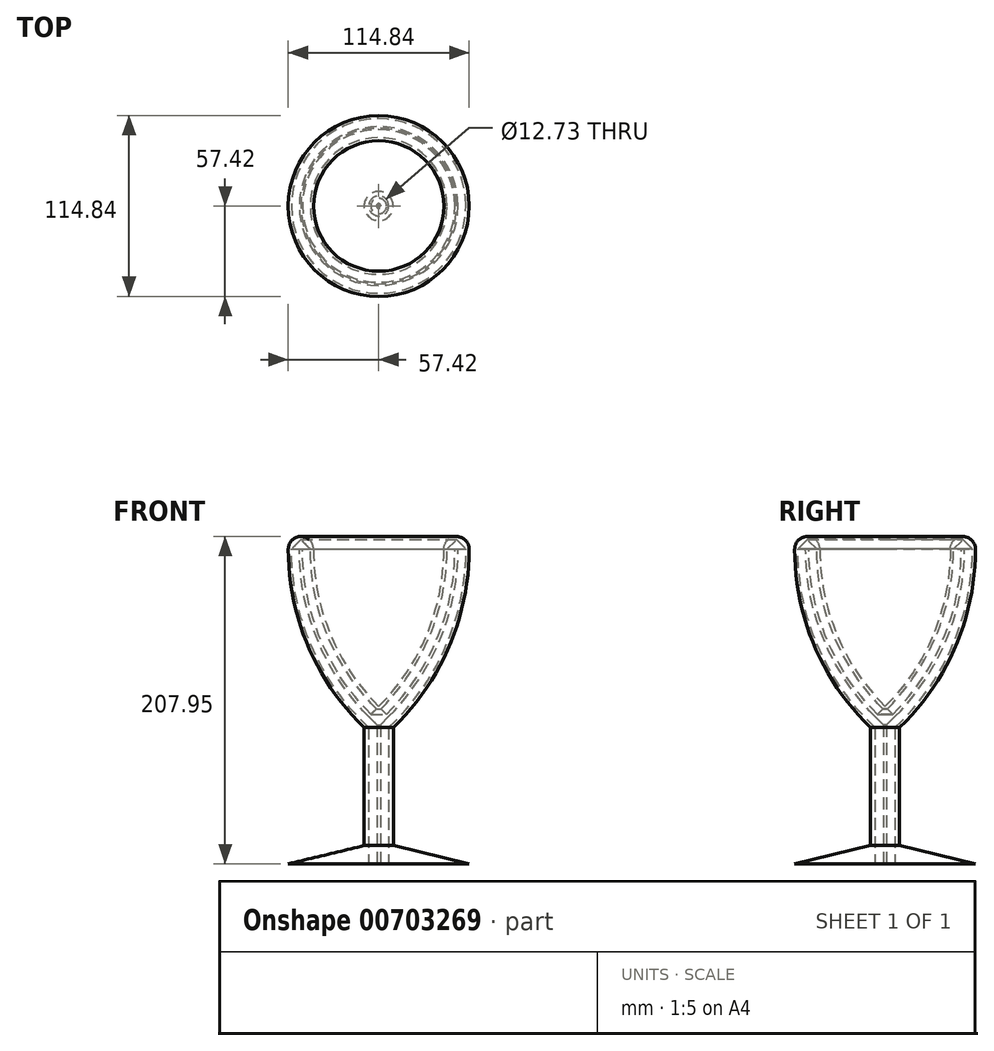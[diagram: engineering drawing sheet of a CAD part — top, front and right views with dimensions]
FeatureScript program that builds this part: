
annotation { "Feature Type Name" : "Feature", "Feature Type Description" : "" }
export const myFeature = defineFeature(function(context is Context, id is Id, definition is map)
    precondition{}
    {
        {
            var Q0;
            Q0=qCreatedBy(makeId("Front.planeOp"),FACE);
            var sketch = newSketch(context, id + "F0", { "sketchPlane" : qUnion([Q0])});
            skArc(sketch, "E0", {"start": v(-41.42, 100) * mm, "mid": v(-30.66, 45.88) * mm, "end": v(0, 0) * mm});
            skLineSegment(sketch, "E1", {"start": v(0, 0) * mm, "end": v(6.82, -6.82) * mm, "construction": true});
            skArc(sketch, "E2", {"start": v(0, 0) * mm, "mid": v(30.66, 45.88) * mm, "end": v(41.42, 100) * mm});
            skLineSegment(sketch, "E3", {"start": v(-100, 100) * mm, "end": v(0, 100) * mm, "construction": true});
            skLineSegment(sketch, "E4", {"start": v(0, 100) * mm, "end": v(100, 100) * mm, "construction": true});
            skArc(sketch, "E5.0", {"start": v(-43.42, 100) * mm, "mid": v(-32.5, 45.12) * mm, "end": v(-1.41, -1.41) * mm});
            skArc(sketch, "E6.0", {"start": v(1.41, -1.41) * mm, "mid": v(32.5, 45.12) * mm, "end": v(43.42, 100) * mm});
            skLineSegment(sketch, "E7", {"start": v(0, 0) * mm, "end": v(-1.41, -1.41) * mm, "construction": true});
            skLineSegment(sketch, "E8", {"start": v(0, 0) * mm, "end": v(1.41, -1.41) * mm, "construction": true});
            skLineSegment(sketch, "E9", {"start": v(-1.41, -1.41) * mm, "end": v(0, -1.41) * mm, "construction": true});
            skLineSegment(sketch, "E10", {"start": v(0, -1.41) * mm, "end": v(1.41, -1.41) * mm, "construction": true});
            skArc(sketch, "E11.0", {"start": v(-48.42, 100) * mm, "mid": v(-37.12, 43.2) * mm, "end": v(-4.95, -4.95) * mm});
            skArc(sketch, "E12.0", {"start": v(4.95, -4.95) * mm, "mid": v(37.12, 43.2) * mm, "end": v(48.42, 100) * mm});
            skArc(sketch, "E13.0", {"start": v(-50.42, 100) * mm, "mid": v(-38.97, 42.44) * mm, "end": v(-6.36, -6.36) * mm});
            skArc(sketch, "E14.0", {"start": v(6.36, -6.36) * mm, "mid": v(38.97, 42.44) * mm, "end": v(50.42, 100) * mm});
            skLineSegment(sketch, "E15", {"start": v(-1.41, -1.41) * mm, "end": v(-4.95, -4.95) * mm});
            skLineSegment(sketch, "E16", {"start": v(1.41, -1.41) * mm, "end": v(4.95, -4.95) * mm});
            skLineSegment(sketch, "E17", {"start": v(-4.95, -4.95) * mm, "end": v(-6.36, -6.36) * mm, "construction": true});
            skLineSegment(sketch, "E18", {"start": v(4.95, -4.95) * mm, "end": v(6.36, -6.36) * mm, "construction": true});
            skArc(sketch, "E19.0", {"start": v(-55.42, 100) * mm, "mid": v(-42.63, 38.26) * mm, "end": v(-6.36, -13.32) * mm});
            skArc(sketch, "E20.0", {"start": v(6.36, -13.32) * mm, "mid": v(42.63, 38.26) * mm, "end": v(55.42, 100) * mm});
            skArc(sketch, "E21.0", {"start": v(-57.42, 100) * mm, "mid": v(-44.88, 38.43) * mm, "end": v(-9.27, -13.32) * mm});
            skArc(sketch, "E22.0", {"start": v(9.27, -13.32) * mm, "mid": v(44.88, 38.43) * mm, "end": v(57.42, 100) * mm});
            skLineSegment(sketch, "E23", {"start": v(6.36, -6.36) * mm, "end": v(6.36, -13.32) * mm});
            skLineSegment(sketch, "E24", {"start": v(9.27, -13.32) * mm, "end": v(6.36, -13.32) * mm, "construction": true});
            skLineSegment(sketch, "E25", {"start": v(-6.36, -6.36) * mm, "end": v(-6.36, -13.32) * mm});
            skLineSegment(sketch, "E26", {"start": v(-9.27, -13.32) * mm, "end": v(-6.36, -13.32) * mm, "construction": true});
            skLineSegment(sketch, "E27", {"start": v(-55.42, 100) * mm, "end": v(-49.42, 106) * mm});
            skLineSegment(sketch, "E28", {"start": v(-49.42, 106) * mm, "end": v(-43.42, 100) * mm});
            skLineSegment(sketch, "E29", {"start": v(43.42, 100) * mm, "end": v(49.42, 106) * mm});
            skLineSegment(sketch, "E30", {"start": v(49.42, 106) * mm, "end": v(55.42, 100) * mm});
            skArc(sketch, "E31", {"start": v(-41.42, 100) * mm, "mid": v(-49.42, 108) * mm, "end": v(-57.42, 100) * mm});
            skLineSegment(sketch, "E32", {"start": v(-50.42, 100) * mm, "end": v(-48.42, 100) * mm});
            skLineSegment(sketch, "E33", {"start": v(48.42, 100) * mm, "end": v(50.42, 100) * mm});
            skArc(sketch, "E34", {"start": v(57.42, 100) * mm, "mid": v(49.42, 108) * mm, "end": v(41.42, 100) * mm});
            skLineSegment(sketch, "E35", {"start": v(-9.27, -13.32) * mm, "end": v(-9.27, -88.32) * mm});
            skLineSegment(sketch, "E36", {"start": v(-9.27, -88.32) * mm, "end": v(-57.42, -99.95) * mm});
            skLineSegment(sketch, "E37", {"start": v(-57.42, -99.95) * mm, "end": v(-6.36, -99.95) * mm});
            skLineSegment(sketch, "E38", {"start": v(6.36, -99.95) * mm, "end": v(57.42, -99.95) * mm});
            skLineSegment(sketch, "E39", {"start": v(57.42, -99.95) * mm, "end": v(9.27, -88.32) * mm});
            skLineSegment(sketch, "E40", {"start": v(9.27, -88.32) * mm, "end": v(9.27, -13.32) * mm});
            skLineSegment(sketch, "E41", {"start": v(-6.36, -13.32) * mm, "end": v(0, -13.32) * mm, "construction": true});
            skLineSegment(sketch, "E42", {"start": v(0, -13.32) * mm, "end": v(6.36, -13.32) * mm, "construction": true});
            skLineSegment(sketch, "E43", {"start": v(-6.36, -13.32) * mm, "end": v(-6.36, -99.95) * mm});
            skLineSegment(sketch, "E44", {"start": v(6.36, -13.32) * mm, "end": v(6.36, -99.95) * mm});
            skLineSegment(sketch, "E45", {"start": v(-6.36, -6.36) * mm, "end": v(6.36, -6.36) * mm});
            skLineSegment(sketch, "E46", {"start": v(0, 0) * mm, "end": v(0, -6.36) * mm});
            skLineSegment(sketch, "E47", {"start": v(-6.36, -6.36) * mm, "end": v(-1, -11.73) * mm});
            skLineSegment(sketch, "E48", {"start": v(-1, -11.73) * mm, "end": v(-1, -99.95) * mm});
            skLineSegment(sketch, "E49", {"start": v(-1, -99.95) * mm, "end": v(0, -99.95) * mm});
            skLineSegment(sketch, "E50", {"start": v(0, -99.95) * mm, "end": v(0, -6.36) * mm});
            skSolve(sketch);
        }
        {
            var Q0;
            Q0=makeQuery(id+"F0.imprint","IMPRINT",FACE,{"disambiguationData":[TD([[makeQuery(id+"F0.imprint","IMPRINT",EDGE,{"derivedFrom":sQuery(id+"F0.wireOp",EDGE,"E0")}),-1.0]])]});
            var Q1;
            {var subQ0=sQuery(id+"F0.wireOp",EDGE,"E47");Q1=makeQuery(id+"F0.imprint","IMPRINT",FACE,{"disambiguationData":[TD([[makeQuery(id+"F0.imprint","IMPRINT",EDGE,{"derivedFrom":subQ0}),1.0]])]});}
            var Q2;
            Q2=sQuery(id+"F0.wireOp",EDGE,"E50");
            revolve(context, id + "F1", {"surfaceOperationType" : NewSurfaceOperationType.NEW, "entities" : qUnion([Q0, Q1]), "axis" : qUnion([Q2]), "revolveType" : RevolveType.FULL});
        }
    });
